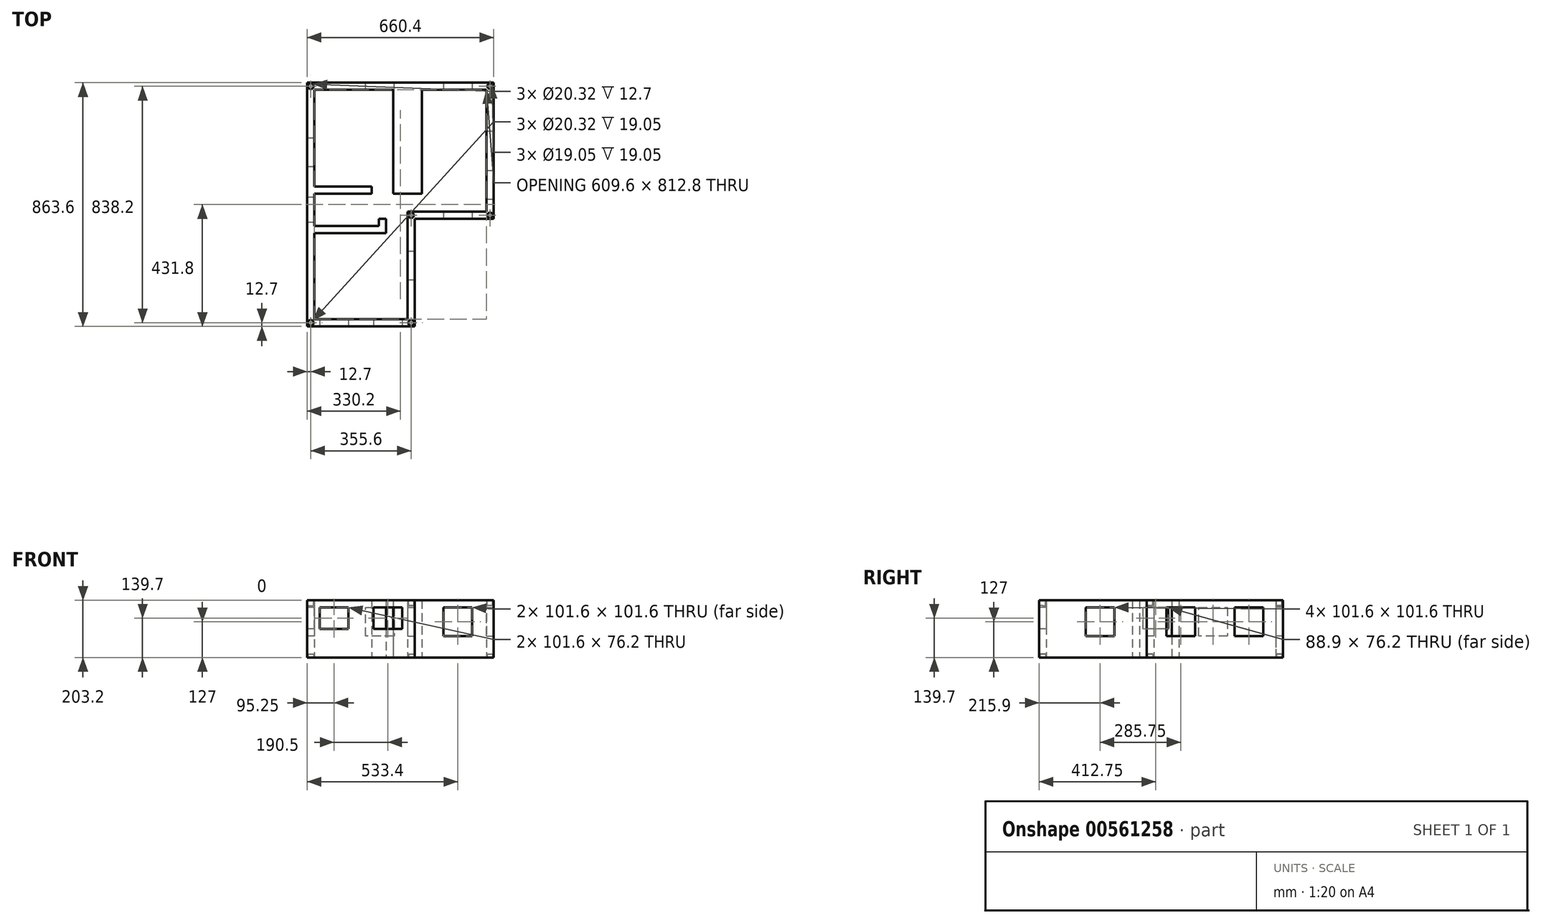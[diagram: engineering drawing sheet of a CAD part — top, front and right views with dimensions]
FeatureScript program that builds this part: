
annotation { "Feature Type Name" : "Feature", "Feature Type Description" : "" }
export const myFeature = defineFeature(function(context is Context, id is Id, definition is map)
    precondition{}
    {
        {
            var Q0;
            Q0=qCreatedBy(makeId("Top.planeOp"),FACE);
            var sketch = newSketch(context, id + "F0", { "sketchPlane" : qUnion([Q0])});
            skLineSegment(sketch, "E0", {"start": v(0, 0) * mm, "end": v(0, 863.6) * mm});
            skLineSegment(sketch, "E1", {"start": v(0, 0) * mm, "end": v(381, 0) * mm});
            skLineSegment(sketch, "E2", {"start": v(381, 0) * mm, "end": v(381, 381) * mm});
            skLineSegment(sketch, "E3", {"start": v(381, 381) * mm, "end": v(660.4, 381) * mm});
            skLineSegment(sketch, "E4", {"start": v(660.4, 381) * mm, "end": v(660.4, 863.6) * mm});
            skLineSegment(sketch, "E5", {"start": v(660.4, 863.6) * mm, "end": v(0, 863.6) * mm});
            skLineSegment(sketch, "E6", {"start": v(25.4, 838.2) * mm, "end": v(25.4, 38.77) * mm});
            skLineSegment(sketch, "E7", {"start": v(25.4, 838.2) * mm, "end": v(660.4, 838.2) * mm});
            skLineSegment(sketch, "E8", {"start": v(660.4, 838.2) * mm, "end": v(660.4, 406.4) * mm});
            skLineSegment(sketch, "E9", {"start": v(355.6, 406.4) * mm, "end": v(355.6, 25.4) * mm});
            skLineSegment(sketch, "E10", {"start": v(355.6, 25.4) * mm, "end": v(25.4, 25.4) * mm});
            skLineSegment(sketch, "E11", {"start": v(25.4, 25.4) * mm, "end": v(25.4, 38.77) * mm});
            skLineSegment(sketch, "E12", {"start": v(25.4, 25.4) * mm, "end": v(25.4, 355.6) * mm});
            skLineSegment(sketch, "E13", {"start": v(406.4, 469.9) * mm, "end": v(406.4, 838.2) * mm});
            skLineSegment(sketch, "E14", {"start": v(304.8, 469.9) * mm, "end": v(304.8, 838.2) * mm});
            skLineSegment(sketch, "E15", {"start": v(279.4, 355.6) * mm, "end": v(279.4, 381) * mm});
            skLineSegment(sketch, "E16", {"start": v(228.6, 469.9) * mm, "end": v(25.4, 469.9) * mm});
            skLineSegment(sketch, "E17", {"start": v(228.6, 469.9) * mm, "end": v(228.6, 495.3) * mm});
            skLineSegment(sketch, "E18", {"start": v(228.6, 495.3) * mm, "end": v(25.4, 495.3) * mm});
            skLineSegment(sketch, "E19", {"start": v(304.8, 469.9) * mm, "end": v(406.4, 469.9) * mm});
            skLineSegment(sketch, "E20", {"start": v(25.4, 355.6) * mm, "end": v(25.4, 330.2) * mm});
            skLineSegment(sketch, "E21", {"start": v(25.4, 330.2) * mm, "end": v(279.4, 330.2) * mm});
            skLineSegment(sketch, "E22", {"start": v(279.4, 330.2) * mm, "end": v(279.4, 355.6) * mm});
            skLineSegment(sketch, "E23", {"start": v(279.4, 381) * mm, "end": v(254, 381) * mm});
            skLineSegment(sketch, "E24", {"start": v(254, 381) * mm, "end": v(254, 355.6) * mm});
            skLineSegment(sketch, "E25", {"start": v(254, 355.6) * mm, "end": v(25.4, 355.6) * mm});
            skLineSegment(sketch, "E26", {"start": v(660.4, 838.2) * mm, "end": v(635, 838.2) * mm});
            skLineSegment(sketch, "E27", {"start": v(635, 838.2) * mm, "end": v(635, 406.4) * mm});
            skLineSegment(sketch, "E28", {"start": v(635, 406.4) * mm, "end": v(355.6, 406.4) * mm});
            skSolve(sketch);
        }
        {
            var Q0;
            Q0=makeQuery(id+"F0.imprint","IMPRINT",FACE,{"disambiguationData":[TD([[makeQuery(id+"F0.imprint","IMPRINT",EDGE,{"derivedFrom":sQuery(id+"F0.wireOp",EDGE,"E15")}),1.0]])]});
            var Q1;
            {var subQ0=sQuery(id+"F0.wireOp",EDGE,"E16");Q1=makeQuery(id+"F0.imprint","IMPRINT",FACE,{"disambiguationData":[TD([[makeQuery(id+"F0.imprint","IMPRINT",EDGE,{"derivedFrom":subQ0}),-1.0]])]});}
            var Q2;
            Q2=makeQuery(id+"F0.imprint","IMPRINT",FACE,{"disambiguationData":[TD([[makeQuery(id+"F0.imprint","IMPRINT",EDGE,{"derivedFrom":sQuery(id+"F0.wireOp",EDGE,"E0")}),-1.0]])]});
            var Q3;
            {var subQ0=sQuery(id+"F0.wireOp",EDGE,"E13");Q3=makeQuery(id+"F0.imprint","IMPRINT",FACE,{"disambiguationData":[TD([[makeQuery(id+"F0.imprint","IMPRINT",EDGE,{"derivedFrom":subQ0}),1.0]])]});}
            extrude(context, id + "F1", {"entities" : qUnion([Q0, Q1, Q2, Q3]), "depth" : 203.2 * mm, "offsetDistance" : 25.4 * mm});
        }
        {
            var Q0;
            Q0=makeQuery(id+"F1.opExtrude","CAP_FACE",FACE,{"disambiguationData":[OSD([sQuery(id+"F0.wireOp",EDGE,"E0"),sQuery(id+"F0.wireOp",EDGE,"E1"),sQuery(id+"F0.wireOp",EDGE,"E2"),sQuery(id+"F0.wireOp",EDGE,"E3"),sQuery(id+"F0.wireOp",EDGE,"E4"),sQuery(id+"F0.wireOp",EDGE,"E5"),sQuery(id+"F0.wireOp",EDGE,"E6"),sQuery(id+"F0.wireOp",EDGE,"E7"),sQuery(id+"F0.wireOp",EDGE,"E8"),sQuery(id+"F0.wireOp",EDGE,"dkMkwTD6-gDEy-1fR3-7D0h-WsMchBQC8n1I"),sQuery(id+"F0.wireOp",EDGE,"E9"),sQuery(id+"F0.wireOp",EDGE,"E10"),sQuery(id+"F0.wireOp",EDGE,"E12"),sQuery(id+"F0.wireOp",EDGE,"a5L4eIkX-EvLa-aPuF-0LoL-EpNOPWYU2y1P"),sQuery(id+"F0.wireOp",EDGE,"E13"),sQuery(id+"F0.wireOp",EDGE,"E14"),sQuery(id+"F0.wireOp",EDGE,"E15"),sQuery(id+"F0.wireOp",EDGE,"E16"),sQuery(id+"F0.wireOp",EDGE,"E17"),sQuery(id+"F0.wireOp",EDGE,"E18"),sQuery(id+"F0.wireOp",EDGE,"E19"),sQuery(id+"F0.wireOp",EDGE,"E21"),sQuery(id+"F0.wireOp",EDGE,"E22"),sQuery(id+"F0.wireOp",EDGE,"E23"),sQuery(id+"F0.wireOp",EDGE,"E24"),sQuery(id+"F0.wireOp",EDGE,"E25")])],"isStart":true});
            var sketch = newSketch(context, id + "F2", { "sketchPlane" : qUnion([Q0])});
            skLineSegment(sketch, "E29", {"start": v(25.4, -838.2) * mm, "end": v(0, -838.2) * mm});
            skLineSegment(sketch, "E30", {"start": v(25.4, -838.2) * mm, "end": v(25.4, -863.6) * mm});
            skLineSegment(sketch, "E31", {"start": v(660.4, -838.2) * mm, "end": v(25.4, -838.2) * mm});
            skLineSegment(sketch, "E32", {"start": v(0, -25.4) * mm, "end": v(25.4, -25.4) * mm});
            skLineSegment(sketch, "E33", {"start": v(25.4, -25.4) * mm, "end": v(25.4, 0) * mm});
            skLineSegment(sketch, "E34", {"start": v(355.6, -25.4) * mm, "end": v(355.6, 0) * mm});
            skLineSegment(sketch, "E35", {"start": v(355.6, -25.4) * mm, "end": v(381, -25.4) * mm});
            skCircle(sketch, "E36", {"center": v(12.7, -850.9) * mm, "radius": 10.16 * mm});
            skPoint(sketch, "E36.centerSnap0", {"position": v(25.4, -850.9) * mm});
            skPoint(sketch, "E36.centerSnap1", {"position": v(12.7, -838.2) * mm});
            skCircle(sketch, "E37", {"center": v(12.7, -12.7) * mm, "radius": 10.16 * mm});
            skPoint(sketch, "E37.centerSnap0", {"position": v(25.4, -12.7) * mm});
            skPoint(sketch, "E37.centerSnap1", {"position": v(12.7, -25.4) * mm});
            skPoint(sketch, "E38.centerSnap0", {"position": v(368.3, -25.4) * mm});
            skPoint(sketch, "E38.centerSnap1", {"position": v(355.6, -12.7) * mm});
            skCircle(sketch, "E39", {"center": v(368.3, -12.7) * mm, "radius": 10.16 * mm});
            skLineSegment(sketch, "E40", {"start": v(635, -838.2) * mm, "end": v(635, -863.6) * mm});
            skLineSegment(sketch, "E41", {"start": v(635, -838.2) * mm, "end": v(660.4, -838.2) * mm});
            skCircle(sketch, "E42", {"center": v(647.7, -850.9) * mm, "radius": 9.53 * mm});
            skPoint(sketch, "E42.centerSnap0", {"position": v(635, -850.9) * mm});
            skPoint(sketch, "E42.centerSnap1", {"position": v(647.7, -838.2) * mm});
            skLineSegment(sketch, "E43", {"start": v(381, -381) * mm, "end": v(355.6, -381) * mm});
            skLineSegment(sketch, "E44", {"start": v(381, -381) * mm, "end": v(381, -406.4) * mm});
            skLineSegment(sketch, "E45", {"start": v(635, -406.4) * mm, "end": v(635, -381) * mm});
            skLineSegment(sketch, "E46", {"start": v(635, -406.4) * mm, "end": v(660.4, -406.4) * mm});
            skCircle(sketch, "E47", {"center": v(368.3, -393.7) * mm, "radius": 9.53 * mm});
            skPoint(sketch, "E47.centerSnap0", {"position": v(381, -393.7) * mm});
            skPoint(sketch, "E47.centerSnap1", {"position": v(368.3, -381) * mm});
            skCircle(sketch, "E48", {"center": v(647.7, -393.7) * mm, "radius": 9.53 * mm});
            skPoint(sketch, "E48.centerSnap0", {"position": v(647.7, -406.4) * mm});
            skPoint(sketch, "E48.centerSnap1", {"position": v(635, -393.7) * mm});
            skSolve(sketch);
        }
        {
            var Q0;
            Q0 = qSketchRegion(id + "F2", true);
            extrude(context, id + "F3", {"entities" : qUnion([Q0]), "operationType" : NewBodyOperationType.REMOVE, "oppositeDirection" : true, "depth" : 12.7 * mm, "offsetDistance" : 25.4 * mm});
        }
        {
            var Q0;
            Q0=makeQuery(id+"F3.boolean.opBoolean","COPY",FACE,{"derivedFrom":makeQuery(id+"F3.opExtrude","CAP_FACE",FACE,{"disambiguationData":[OSD([sQuery(id+"F2.wireOp",EDGE,"E37")])],"isStart":false})});
            var Q1;
            Q1=makeQuery(id+"F3.boolean.opBoolean","COPY",FACE,{"derivedFrom":makeQuery(id+"F3.opExtrude","CAP_FACE",FACE,{"disambiguationData":[OSD([sQuery(id+"F2.wireOp",EDGE,"E39")])],"isStart":false})});
            var Q2;
            Q2=makeQuery(id+"F3.boolean.opBoolean","COPY",FACE,{"derivedFrom":makeQuery(id+"F3.opExtrude","CAP_FACE",FACE,{"disambiguationData":[OSD([sQuery(id+"F2.wireOp",EDGE,"LHl6VvYp-uiVD-yo0g-14rr-IgKT87OaGdYD")])],"isStart":false})});
            var Q3;
            Q3=makeQuery(id+"F3.boolean.opBoolean","COPY",FACE,{"derivedFrom":makeQuery(id+"F3.opExtrude","CAP_FACE",FACE,{"disambiguationData":[OSD([sQuery(id+"F2.wireOp",EDGE,"anxL4029-Ef43-RbmJ-oOy6-QRB82zmBKlNa")])],"isStart":false})});
            var Q4;
            Q4=makeQuery(id+"F3.boolean.opBoolean","COPY",FACE,{"derivedFrom":makeQuery(id+"F3.opExtrude","CAP_FACE",FACE,{"disambiguationData":[OSD([sQuery(id+"F2.wireOp",EDGE,"E36")])],"isStart":false})});
            var Q5;
            Q5=makeQuery(id+"F3.boolean.opBoolean","COPY",FACE,{"derivedFrom":makeQuery(id+"F3.opExtrude","CAP_FACE",FACE,{"disambiguationData":[OSD([sQuery(id+"F2.wireOp",EDGE,"oE6opEG0-J6x6-MSJh-WqTT-orI0GwdiHoFM")])],"isStart":false})});
            extrude(context, id + "F4", {"entities" : qUnion([Q0, Q1, Q2, Q3, Q4, Q5]), "operationType" : NewBodyOperationType.ADD, "oppositeDirection" : true, "depth" : 203.2 * mm, "offsetDistance" : 25.4 * mm});
        }
        {
            var Q0;
            Q0=makeQuery(id+"F4.opExtrude","CAP_FACE",FACE,{"disambiguationData":[OSD([sQuery(id+"F2.wireOp",EDGE,"E36")])],"isStart":false});
            var Q1;
            Q1=makeQuery(id+"F4.opExtrude","CAP_FACE",FACE,{"disambiguationData":[OSD([sQuery(id+"F2.wireOp",EDGE,"oE6opEG0-J6x6-MSJh-WqTT-orI0GwdiHoFM")])],"isStart":false});
            var Q2;
            Q2=makeQuery(id+"F4.opExtrude","CAP_FACE",FACE,{"disambiguationData":[OSD([sQuery(id+"F2.wireOp",EDGE,"anxL4029-Ef43-RbmJ-oOy6-QRB82zmBKlNa")])],"isStart":false});
            var Q3;
            Q3=makeQuery(id+"F4.opExtrude","CAP_FACE",FACE,{"disambiguationData":[OSD([sQuery(id+"F2.wireOp",EDGE,"LHl6VvYp-uiVD-yo0g-14rr-IgKT87OaGdYD")])],"isStart":false});
            var Q4;
            Q4=makeQuery(id+"F4.opExtrude","CAP_FACE",FACE,{"disambiguationData":[OSD([sQuery(id+"F2.wireOp",EDGE,"E39")])],"isStart":false});
            var Q5;
            Q5=makeQuery(id+"F4.opExtrude","CAP_FACE",FACE,{"disambiguationData":[OSD([sQuery(id+"F2.wireOp",EDGE,"E37")])],"isStart":false});
            extrude(context, id + "F5", {"entities" : qUnion([Q0, Q1, Q2, Q3, Q4, Q5]), "operationType" : NewBodyOperationType.REMOVE, "oppositeDirection" : true, "depth" : 31.75 * mm, "offsetDistance" : 25.4 * mm});
        }
        {
            var Q0;
            Q0=makeQuery(id+"F1.opExtrude","SWEPT_FACE",FACE,{"disambiguationData":[OSD([sQuery(id+"F0.wireOp",EDGE,"E1")])]});
            var sketch = newSketch(context, id + "F6", { "sketchPlane" : qUnion([Q0])});
            skLineSegment(sketch, "E49", {"start": v(0, 203.2) * mm, "end": v(381, 203.2) * mm});
            skLineSegment(sketch, "E50", {"start": v(381, 203.2) * mm, "end": v(381, 0) * mm});
            skLineSegment(sketch, "E51", {"start": v(381, 0) * mm, "end": v(0, 0) * mm});
            skLineSegment(sketch, "E52", {"start": v(0, 0) * mm, "end": v(0, 203.2) * mm});
            skLineSegment(sketch, "E53", {"start": v(190.5, 203.2) * mm, "end": v(190.5, 0) * mm});
            skLineSegment(sketch, "E54", {"start": v(95.25, 101.6) * mm, "end": v(95.25, 177.8) * mm});
            skPoint(sketch, "E54.endSnap0", {"position": v(95.25, 101.6) * mm});
            skLineSegment(sketch, "E55", {"start": v(95.25, 177.8) * mm, "end": v(44.45, 177.8) * mm});
            skLineSegment(sketch, "E56", {"start": v(44.45, 177.8) * mm, "end": v(44.45, 101.6) * mm});
            skLineSegment(sketch, "E57", {"start": v(44.45, 101.6) * mm, "end": v(146.05, 101.6) * mm});
            skLineSegment(sketch, "E58", {"start": v(146.05, 101.6) * mm, "end": v(146.05, 177.8) * mm});
            skLineSegment(sketch, "E59", {"start": v(146.05, 177.8) * mm, "end": v(95.25, 177.8) * mm});
            skLineSegment(sketch, "E60.MirrorCS", {"start": v(234.95, 101.6) * mm, "end": v(234.95, 177.8) * mm});
            skLineSegment(sketch, "E61.MirrorCS", {"start": v(336.55, 177.8) * mm, "end": v(336.55, 101.6) * mm});
            skLineSegment(sketch, "E62.MirrorCS", {"start": v(234.95, 177.8) * mm, "end": v(285.75, 177.8) * mm});
            skLineSegment(sketch, "E63.MirrorCS", {"start": v(285.75, 177.8) * mm, "end": v(336.55, 177.8) * mm});
            skLineSegment(sketch, "E64.MirrorCS", {"start": v(336.55, 101.6) * mm, "end": v(234.95, 101.6) * mm});
            skSolve(sketch);
        }
        {
            var Q0;
            {var subQ0=sQuery(id+"F6.wireOp",EDGE,"E54");Q0=makeQuery(id+"F6.imprint","IMPRINT",FACE,{"disambiguationData":[TD([[makeQuery(id+"F6.imprint","IMPRINT",EDGE,{"derivedFrom":subQ0}),-1.0]])]});}
            var Q1;
            {var subQ0=sQuery(id+"F6.wireOp",EDGE,"E54");Q1=makeQuery(id+"F6.imprint","IMPRINT",FACE,{"disambiguationData":[TD([[makeQuery(id+"F6.imprint","IMPRINT",EDGE,{"derivedFrom":subQ0}),1.0]])]});}
            var Q2;
            Q2=makeQuery(id+"F6.imprint","IMPRINT",FACE,{"disambiguationData":[TD([[makeQuery(id+"F6.imprint","IMPRINT",EDGE,{"derivedFrom":sQuery(id+"F6.wireOp",EDGE,"E60.MirrorCS")}),-1.0]])]});
            extrude(context, id + "F7", {"entities" : qUnion([Q0, Q1, Q2]), "operationType" : NewBodyOperationType.REMOVE, "oppositeDirection" : true, "depth" : 25.4 * mm, "offsetDistance" : 25.4 * mm});
        }
        {
            var Q0;
            Q0=makeQuery(id+"F1.opExtrude","SWEPT_FACE",FACE,{"disambiguationData":[OSD([sQuery(id+"F0.wireOp",EDGE,"E2")])]});
            var sketch = newSketch(context, id + "F8", { "sketchPlane" : qUnion([Q0])});
            skLineSegment(sketch, "E65", {"start": v(0, 203.2) * mm, "end": v(0, 0) * mm});
            skLineSegment(sketch, "E66", {"start": v(0, 0) * mm, "end": v(381, 0) * mm});
            skLineSegment(sketch, "E67", {"start": v(381, 0) * mm, "end": v(381, 203.2) * mm});
            skLineSegment(sketch, "E68", {"start": v(381, 203.2) * mm, "end": v(0, 203.2) * mm});
            skLineSegment(sketch, "E69", {"start": v(190.5, 76.2) * mm, "end": v(165.1, 76.2) * mm});
            skPoint(sketch, "E69.endSnap0", {"position": v(190.5, 76.2) * mm});
            skLineSegment(sketch, "E70", {"start": v(165.1, 76.2) * mm, "end": v(165.1, 177.8) * mm});
            skLineSegment(sketch, "E71", {"start": v(165.1, 177.8) * mm, "end": v(266.7, 177.8) * mm});
            skLineSegment(sketch, "E72", {"start": v(266.7, 177.8) * mm, "end": v(266.7, 76.2) * mm});
            skLineSegment(sketch, "E73", {"start": v(266.7, 76.2) * mm, "end": v(190.5, 76.2) * mm});
            skSolve(sketch);
        }
        {
            var Q0;
            Q0=makeQuery(id+"F8.imprint","IMPRINT",FACE,{"disambiguationData":[TD([[makeQuery(id+"F8.imprint","IMPRINT",EDGE,{"derivedFrom":sQuery(id+"F8.wireOp",EDGE,"E69")}),-1.0]])]});
            extrude(context, id + "F9", {"entities" : qUnion([Q0]), "operationType" : NewBodyOperationType.REMOVE, "oppositeDirection" : true, "depth" : 25.4 * mm, "offsetDistance" : 25.4 * mm});
        }
        {
            var Q0;
            Q0=makeQuery(id+"F1.opExtrude","SWEPT_FACE",FACE,{"disambiguationData":[OSD([sQuery(id+"F0.wireOp",EDGE,"E3")])]});
            var sketch = newSketch(context, id + "F10", { "sketchPlane" : qUnion([Q0])});
            skLineSegment(sketch, "E74", {"start": v(381, 203.2) * mm, "end": v(381, 0) * mm});
            skLineSegment(sketch, "E75", {"start": v(381, 0) * mm, "end": v(660.4, 0) * mm});
            skLineSegment(sketch, "E76", {"start": v(660.4, 0) * mm, "end": v(660.4, 203.2) * mm});
            skLineSegment(sketch, "E77", {"start": v(660.4, 203.2) * mm, "end": v(381, 203.2) * mm});
            skLineSegment(sketch, "E78", {"start": v(533.4, 76.2) * mm, "end": v(482.6, 76.2) * mm});
            skLineSegment(sketch, "E79", {"start": v(482.6, 76.2) * mm, "end": v(482.6, 177.8) * mm});
            skLineSegment(sketch, "E80", {"start": v(482.6, 177.8) * mm, "end": v(584.2, 177.8) * mm});
            skLineSegment(sketch, "E81", {"start": v(584.2, 177.8) * mm, "end": v(584.2, 76.2) * mm});
            skLineSegment(sketch, "E82", {"start": v(584.2, 76.2) * mm, "end": v(533.4, 76.2) * mm});
            skSolve(sketch);
        }
        {
            var Q0;
            Q0=makeQuery(id+"F10.imprint","IMPRINT",FACE,{"disambiguationData":[TD([[makeQuery(id+"F10.imprint","IMPRINT",EDGE,{"derivedFrom":sQuery(id+"F10.wireOp",EDGE,"E78")}),-1.0]])]});
            extrude(context, id + "F11", {"entities" : qUnion([Q0]), "operationType" : NewBodyOperationType.REMOVE, "oppositeDirection" : true, "depth" : 2540 * mm, "offsetDistance" : 25.4 * mm});
        }
        {
            var Q0;
            Q0=makeQuery(id+"F1.opExtrude","SWEPT_FACE",FACE,{"disambiguationData":[OSD([sQuery(id+"F0.wireOp",EDGE,"E4")])]});
            var sketch = newSketch(context, id + "F12", { "sketchPlane" : qUnion([Q0])});
            skLineSegment(sketch, "E83", {"start": v(381, 203.2) * mm, "end": v(381, 0) * mm});
            skLineSegment(sketch, "E84", {"start": v(381, 0) * mm, "end": v(863.6, 0) * mm});
            skLineSegment(sketch, "E85", {"start": v(863.6, 0) * mm, "end": v(863.6, 203.2) * mm});
            skLineSegment(sketch, "E86", {"start": v(863.6, 203.2) * mm, "end": v(381, 203.2) * mm});
            skLineSegment(sketch, "E87", {"start": v(622.3, 203.2) * mm, "end": v(622.3, 0) * mm});
            skLineSegment(sketch, "E88", {"start": v(381, 0) * mm, "end": v(622.3, 0) * mm});
            skLineSegment(sketch, "E89", {"start": v(622.3, 0) * mm, "end": v(863.6, 0) * mm});
            skLineSegment(sketch, "E90", {"start": v(501.65, 76.2) * mm, "end": v(450.85, 76.2) * mm});
            skLineSegment(sketch, "E91", {"start": v(450.85, 76.2) * mm, "end": v(450.85, 177.8) * mm});
            skLineSegment(sketch, "E92", {"start": v(450.85, 177.8) * mm, "end": v(552.45, 177.8) * mm});
            skLineSegment(sketch, "E93", {"start": v(552.45, 177.8) * mm, "end": v(552.45, 76.2) * mm});
            skLineSegment(sketch, "E94", {"start": v(552.45, 76.2) * mm, "end": v(501.65, 76.2) * mm});
            skLineSegment(sketch, "E95.MirrorCS", {"start": v(692.15, 177.8) * mm, "end": v(692.15, 76.2) * mm});
            skLineSegment(sketch, "E96.MirrorCS", {"start": v(692.15, 76.2) * mm, "end": v(742.95, 76.2) * mm});
            skLineSegment(sketch, "E97.MirrorCS", {"start": v(742.95, 76.2) * mm, "end": v(793.75, 76.2) * mm});
            skLineSegment(sketch, "E98.MirrorCS", {"start": v(793.75, 76.2) * mm, "end": v(793.75, 177.8) * mm});
            skLineSegment(sketch, "E99.MirrorCS", {"start": v(793.75, 177.8) * mm, "end": v(692.15, 177.8) * mm});
            skSolve(sketch);
        }
        {
            var Q0;
            Q0=makeQuery(id+"F12.imprint","IMPRINT",FACE,{"disambiguationData":[TD([[makeQuery(id+"F12.imprint","IMPRINT",EDGE,{"derivedFrom":sQuery(id+"F12.wireOp",EDGE,"E90")}),-1.0]])]});
            var Q1;
            Q1=makeQuery(id+"F12.imprint","IMPRINT",FACE,{"disambiguationData":[TD([[makeQuery(id+"F12.imprint","IMPRINT",EDGE,{"derivedFrom":sQuery(id+"F12.wireOp",EDGE,"E95.MirrorCS")}),1.0]])]});
            extrude(context, id + "F13", {"entities" : qUnion([Q0, Q1]), "operationType" : NewBodyOperationType.REMOVE, "oppositeDirection" : true, "depth" : 25.4 * mm, "offsetDistance" : 25.4 * mm});
        }
        {
            var Q0;
            Q0=makeQuery(id+"F1.opExtrude","SWEPT_FACE",FACE,{"disambiguationData":[OSD([sQuery(id+"F0.wireOp",EDGE,"E5")])]});
            var sketch = newSketch(context, id + "F14", { "sketchPlane" : qUnion([Q0])});
            skLineSegment(sketch, "E100", {"start": v(-660.4, 203.2) * mm, "end": v(0, 203.2) * mm});
            skLineSegment(sketch, "E101", {"start": v(0, 203.2) * mm, "end": v(0, 0) * mm});
            skLineSegment(sketch, "E102", {"start": v(0, 0) * mm, "end": v(-660.4, 0) * mm});
            skLineSegment(sketch, "E103", {"start": v(-660.4, 0) * mm, "end": v(-660.4, 203.2) * mm});
            skLineSegment(sketch, "E104", {"start": v(-330.2, 203.2) * mm, "end": v(-330.2, 0) * mm});
            skLineSegment(sketch, "E105", {"start": v(-660.4, 203.2) * mm, "end": v(-330.2, 203.2) * mm});
            skLineSegment(sketch, "E106", {"start": v(-330.2, 203.2) * mm, "end": v(0, 203.2) * mm});
            skLineSegment(sketch, "E107", {"start": v(-165.1, 203.2) * mm, "end": v(-165.1, 0) * mm});
            skLineSegment(sketch, "E108", {"start": v(-330.2, 203.2) * mm, "end": v(-165.1, 203.2) * mm});
            skLineSegment(sketch, "E109", {"start": v(-257.18, 177.8) * mm, "end": v(-307.98, 177.8) * mm});
            skLineSegment(sketch, "E110", {"start": v(-307.98, 177.8) * mm, "end": v(-307.98, 76.2) * mm});
            skLineSegment(sketch, "E111", {"start": v(-307.98, 76.2) * mm, "end": v(-206.38, 76.2) * mm});
            skLineSegment(sketch, "E112", {"start": v(-206.38, 76.2) * mm, "end": v(-206.38, 177.8) * mm});
            skLineSegment(sketch, "E113", {"start": v(-206.38, 177.8) * mm, "end": v(-257.18, 177.8) * mm});
            skLineSegment(sketch, "E114", {"start": v(-660.4, 203.2) * mm, "end": v(-419.1, 203.2) * mm});
            skLineSegment(sketch, "E115", {"start": v(-565.15, 177.8) * mm, "end": v(-615.95, 177.8) * mm});
            skLineSegment(sketch, "E116", {"start": v(-615.95, 177.8) * mm, "end": v(-615.95, 76.2) * mm});
            skLineSegment(sketch, "E117", {"start": v(-615.95, 76.2) * mm, "end": v(-514.35, 76.2) * mm});
            skLineSegment(sketch, "E118", {"start": v(-514.35, 76.2) * mm, "end": v(-514.35, 177.8) * mm});
            skLineSegment(sketch, "E119", {"start": v(-514.35, 177.8) * mm, "end": v(-565.15, 177.8) * mm});
            skSolve(sketch);
        }
        {
            var Q0;
            Q0=makeQuery(id+"F14.imprint","IMPRINT",FACE,{"disambiguationData":[TD([[makeQuery(id+"F14.imprint","IMPRINT",EDGE,{"derivedFrom":sQuery(id+"F14.wireOp",EDGE,"E109")}),1.0]])]});
            extrude(context, id + "F15", {"entities" : qUnion([Q0]), "operationType" : NewBodyOperationType.REMOVE, "oppositeDirection" : true, "depth" : 25.4 * mm, "offsetDistance" : 25.4 * mm});
        }
        {
            var Q0;
            Q0=makeQuery(id+"F1.opExtrude","SWEPT_FACE",FACE,{"disambiguationData":[OSD([sQuery(id+"F0.wireOp",EDGE,"E0")])]});
            var sketch = newSketch(context, id + "F16", { "sketchPlane" : qUnion([Q0])});
            skLineSegment(sketch, "E120.0", {"start": v(-469.9, 203.2) * mm, "end": v(-355.6, 203.2) * mm});
            skLineSegment(sketch, "E121", {"start": v(-457.2, 177.8) * mm, "end": v(-457.2, 101.6) * mm});
            skLineSegment(sketch, "E122", {"start": v(-457.2, 101.6) * mm, "end": v(-368.3, 101.6) * mm});
            skLineSegment(sketch, "E123", {"start": v(-368.3, 101.6) * mm, "end": v(-368.3, 177.8) * mm});
            skLineSegment(sketch, "E124", {"start": v(-457.2, 177.8) * mm, "end": v(-368.3, 177.8) * mm});
            skLineSegment(sketch, "E125", {"start": v(-863.6, 203.2) * mm, "end": v(-838.2, 203.2) * mm});
            skLineSegment(sketch, "E126", {"start": v(-838.2, 203.2) * mm, "end": v(-495.3, 203.2) * mm});
            skLineSegment(sketch, "E127", {"start": v(-495.3, 203.2) * mm, "end": v(-495.3, 0) * mm});
            skLineSegment(sketch, "E128", {"start": v(-495.3, 0) * mm, "end": v(-863.6, 0) * mm});
            skLineSegment(sketch, "E129", {"start": v(-666.75, 177.8) * mm, "end": v(-666.75, 76.2) * mm});
            skLineSegment(sketch, "E130", {"start": v(-666.75, 76.2) * mm, "end": v(-565.15, 76.2) * mm});
            skLineSegment(sketch, "E131", {"start": v(-565.15, 76.2) * mm, "end": v(-565.15, 177.8) * mm});
            skLineSegment(sketch, "E132", {"start": v(-565.15, 177.8) * mm, "end": v(-666.75, 177.8) * mm});
            skSolve(sketch);
        }
        {
            var Q0;
            Q0=makeQuery(id+"F16.imprint","IMPRINT",FACE,{"disambiguationData":[TD([[makeQuery(id+"F16.imprint","IMPRINT",EDGE,{"derivedFrom":sQuery(id+"F16.wireOp",EDGE,"E121")}),1.0]])]});
            extrude(context, id + "F17", {"entities" : qUnion([Q0]), "operationType" : NewBodyOperationType.REMOVE, "oppositeDirection" : true, "depth" : 25.4 * mm, "offsetDistance" : 25.4 * mm});
        }
        {
            var Q0;
            Q0 = qSketchRegion(id + "F16", true);
            extrude(context, id + "F18", {"entities" : qUnion([Q0]), "operationType" : NewBodyOperationType.REMOVE, "oppositeDirection" : true, "depth" : 25.4 * mm, "offsetDistance" : 25.4 * mm});
        }
        {
            var Q0;
            Q0=makeQuery(id+"F1.opExtrude","CAP_FACE",FACE,{"disambiguationData":[OSD([sQuery(id+"F0.wireOp",EDGE,"E0"),sQuery(id+"F0.wireOp",EDGE,"E1"),sQuery(id+"F0.wireOp",EDGE,"E2"),sQuery(id+"F0.wireOp",EDGE,"E3"),sQuery(id+"F0.wireOp",EDGE,"E4"),sQuery(id+"F0.wireOp",EDGE,"E5"),sQuery(id+"F0.wireOp",EDGE,"E6"),sQuery(id+"F0.wireOp",EDGE,"E7"),sQuery(id+"F0.wireOp",EDGE,"E8"),sQuery(id+"F0.wireOp",EDGE,"E9"),sQuery(id+"F0.wireOp",EDGE,"E10"),sQuery(id+"F0.wireOp",EDGE,"E12"),sQuery(id+"F0.wireOp",EDGE,"E13"),sQuery(id+"F0.wireOp",EDGE,"E14"),sQuery(id+"F0.wireOp",EDGE,"E15"),sQuery(id+"F0.wireOp",EDGE,"E16"),sQuery(id+"F0.wireOp",EDGE,"E17"),sQuery(id+"F0.wireOp",EDGE,"E18"),sQuery(id+"F0.wireOp",EDGE,"E19"),sQuery(id+"F0.wireOp",EDGE,"E21"),sQuery(id+"F0.wireOp",EDGE,"E22"),sQuery(id+"F0.wireOp",EDGE,"E23"),sQuery(id+"F0.wireOp",EDGE,"E24"),sQuery(id+"F0.wireOp",EDGE,"E25"),sQuery(id+"F0.wireOp",EDGE,"E27"),sQuery(id+"F0.wireOp",EDGE,"E28")])],"isStart":false});
            var sketch = newSketch(context, id + "F19", { "sketchPlane" : qUnion([Q0])});
            skLineSegment(sketch, "E133", {"start": v(381, 381) * mm, "end": v(355.6, 381) * mm});
            skLineSegment(sketch, "E134", {"start": v(381, 381) * mm, "end": v(381, 406.4) * mm});
            skLineSegment(sketch, "E135", {"start": v(635, 406.4) * mm, "end": v(635, 381) * mm});
            skLineSegment(sketch, "E136", {"start": v(635, 406.4) * mm, "end": v(660.4, 406.4) * mm});
            skLineSegment(sketch, "E137", {"start": v(635, 838.2) * mm, "end": v(635, 863.6) * mm});
            skLineSegment(sketch, "E138", {"start": v(635, 838.2) * mm, "end": v(660.4, 838.2) * mm});
            skPoint(sketch, "E139.centerSnap0", {"position": v(635, 850.9) * mm});
            skCircle(sketch, "E140", {"center": v(647.7, 850.9) * mm, "radius": 9.53 * mm});
            skPoint(sketch, "E140.centerSnap0", {"position": v(647.7, 838.2) * mm});
            skCircle(sketch, "E141", {"center": v(647.7, 393.7) * mm, "radius": 9.53 * mm});
            skPoint(sketch, "E141.centerSnap0", {"position": v(647.7, 406.4) * mm});
            skPoint(sketch, "E141.centerSnap1", {"position": v(635, 393.7) * mm});
            skCircle(sketch, "E142", {"center": v(368.3, 393.7) * mm, "radius": 9.53 * mm});
            skPoint(sketch, "E142.centerSnap0", {"position": v(381, 393.7) * mm});
            skPoint(sketch, "E142.centerSnap1", {"position": v(368.3, 381) * mm});
            skSolve(sketch);
        }
        {
            var Q0;
            Q0=makeQuery(id+"F19.imprint","IMPRINT",FACE,{"disambiguationData":[TD([[makeQuery(id+"F19.imprint","IMPRINT",EDGE,{"derivedFrom":sQuery(id+"F19.wireOp",EDGE,"E142")}),1.0]])]});
            var Q1;
            Q1=makeQuery(id+"F19.imprint","IMPRINT",FACE,{"disambiguationData":[TD([[makeQuery(id+"F19.imprint","IMPRINT",EDGE,{"derivedFrom":sQuery(id+"F19.wireOp",EDGE,"E141")}),1.0]])]});
            var Q2;
            Q2=makeQuery(id+"F19.imprint","IMPRINT",FACE,{"disambiguationData":[TD([[makeQuery(id+"F19.imprint","IMPRINT",EDGE,{"derivedFrom":sQuery(id+"F19.wireOp",EDGE,"E140")}),1.0]])]});
            extrude(context, id + "F20", {"entities" : qUnion([Q0, Q1, Q2]), "operationType" : NewBodyOperationType.REMOVE, "oppositeDirection" : true, "depth" : 19.05 * mm, "offsetDistance" : 25.4 * mm});
        }
    });
